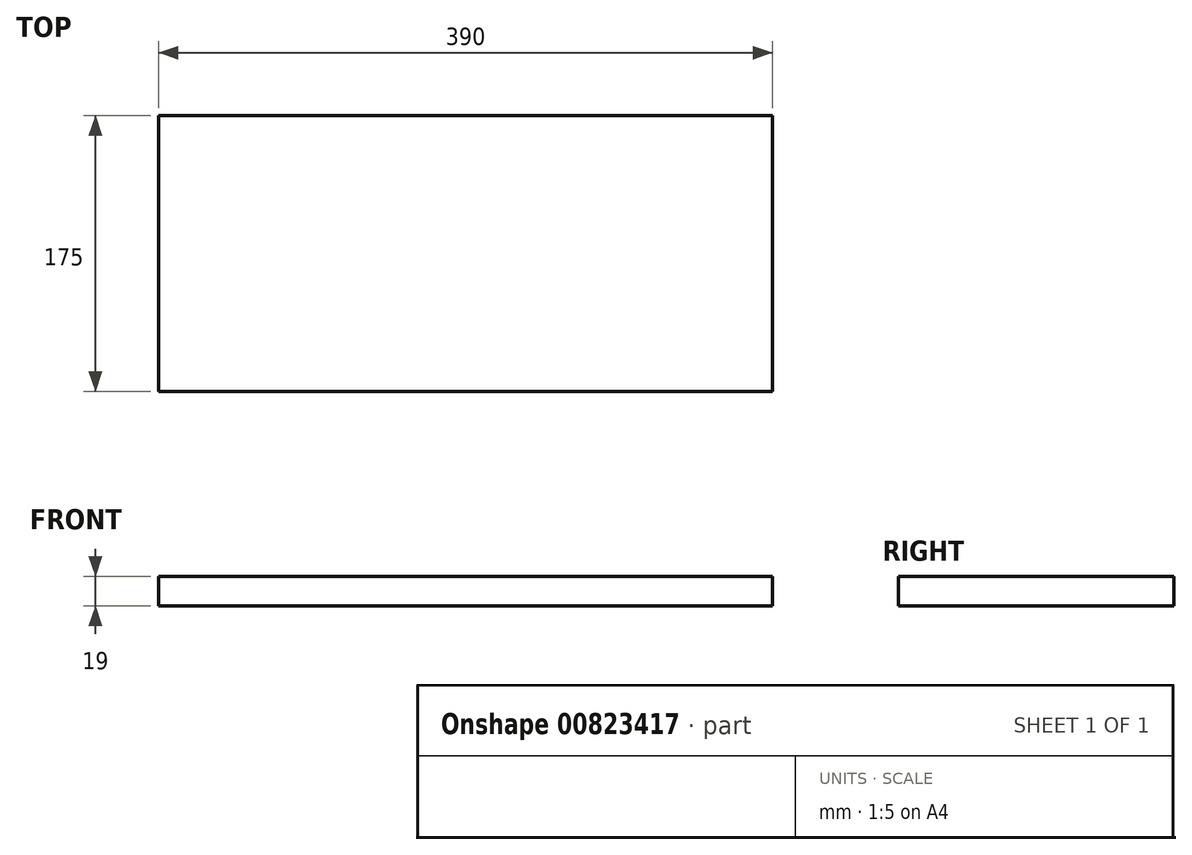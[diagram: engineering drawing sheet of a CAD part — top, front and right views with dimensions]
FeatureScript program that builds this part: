
annotation { "Feature Type Name" : "Feature", "Feature Type Description" : "" }
export const myFeature = defineFeature(function(context is Context, id is Id, definition is map)
    precondition{}
    {
        {
            var Q0;
            Q0=qCreatedBy(makeId("Top.planeOp"),FACE);
            var sketch = newSketch(context, id + "F0", { "sketchPlane" : qUnion([Q0])});
            skLineSegment(sketch, "E0.bottom", {"start": v(-195, 87.5) * mm, "end": v(195, 87.5) * mm});
            skLineSegment(sketch, "E0.top", {"start": v(-195, -87.5) * mm, "end": v(195, -87.5) * mm});
            skLineSegment(sketch, "E0.left", {"start": v(-195, 87.5) * mm, "end": v(-195, -87.5) * mm});
            skLineSegment(sketch, "E0.right", {"start": v(195, 87.5) * mm, "end": v(195, -87.5) * mm});
            skPoint(sketch, "E0.middle", {"position": v(0, 0) * mm});
            skSolve(sketch);
        }
        {
            var Q0;
            Q0=makeQuery(id+"F0.imprint","IMPRINT",FACE,{"disambiguationData":[TD([[makeQuery(id+"F0.imprint","IMPRINT",EDGE,{"derivedFrom":sQuery(id+"F0.wireOp",EDGE,"E0.bottom")}),-1.0]])]});
            extrude(context, id + "F1", {"entities" : qUnion([Q0]), "depth" : 19 * mm, "offsetDistance" : 25 * mm});
        }
    });
